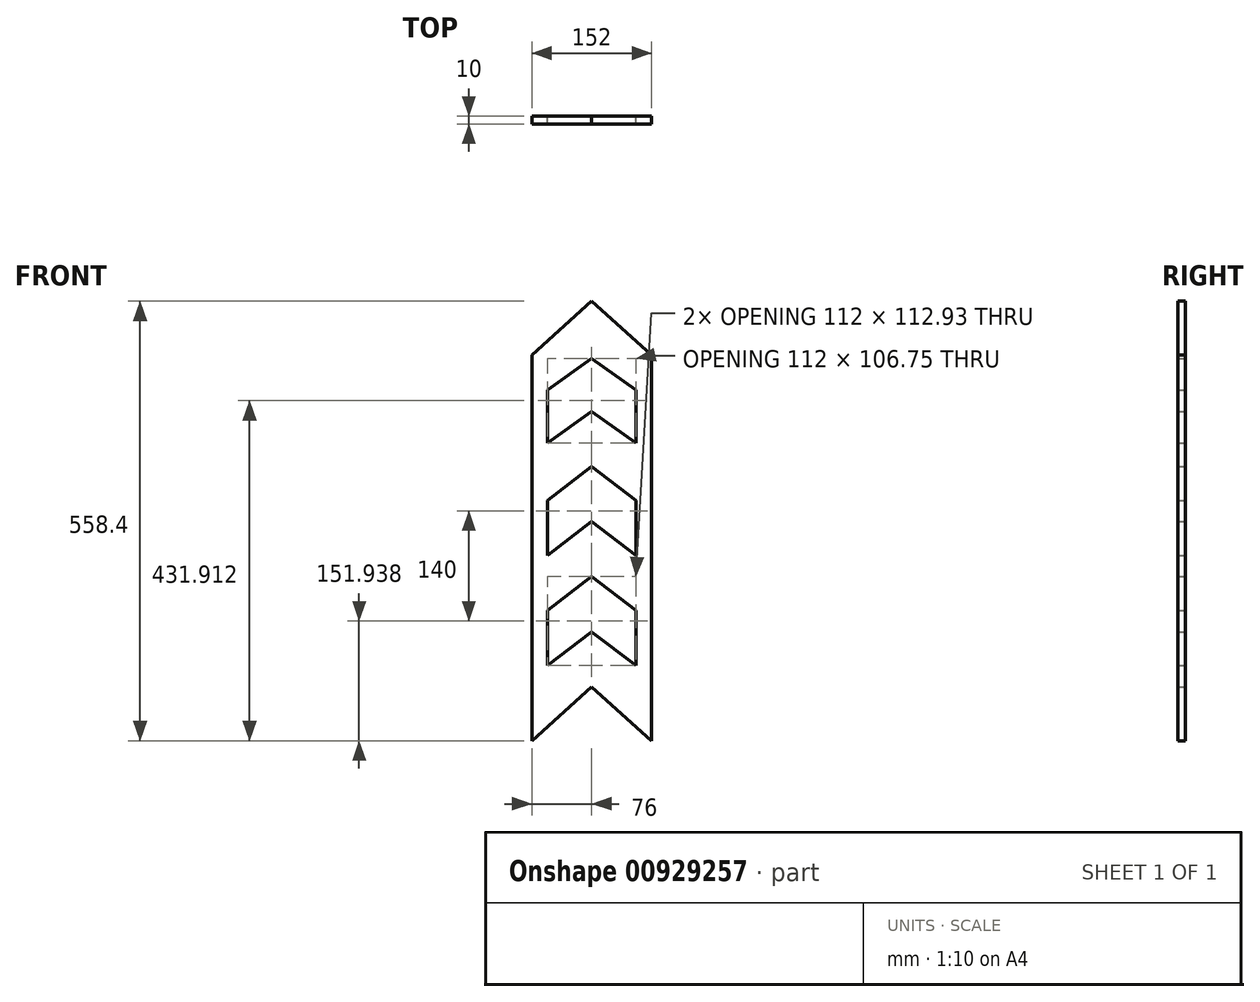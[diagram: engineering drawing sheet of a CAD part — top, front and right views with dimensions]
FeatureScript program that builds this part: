
annotation { "Feature Type Name" : "Feature", "Feature Type Description" : "" }
export const myFeature = defineFeature(function(context is Context, id is Id, definition is map)
    precondition{}
    {
        {
            var Q0;
            Q0=qCreatedBy(makeId("Front.planeOp"),FACE);
            var sketch = newSketch(context, id + "F0", { "sketchPlane" : qUnion([Q0])});
            skLineSegment(sketch, "E0", {"start": v(0, 241.08) * mm, "end": v(-76, 172.68) * mm});
            skLineSegment(sketch, "E1", {"start": v(-76, 172.68) * mm, "end": v(-76, -317.32) * mm});
            skLineSegment(sketch, "E2", {"start": v(-76, -317.32) * mm, "end": v(0, -248.92) * mm});
            skLineSegment(sketch, "E3", {"start": v(0, 167.96) * mm, "end": v(-56, 128.1) * mm});
            skLineSegment(sketch, "E4", {"start": v(-56, 128.1) * mm, "end": v(-56, 61.22) * mm});
            skLineSegment(sketch, "E5", {"start": v(-56, 61.22) * mm, "end": v(0, 101.08) * mm});
            skLineSegment(sketch, "E6", {"start": v(0, 31.08) * mm, "end": v(-56, -11.85) * mm});
            skLineSegment(sketch, "E7", {"start": v(-56, -11.85) * mm, "end": v(-56, -81.85) * mm});
            skLineSegment(sketch, "E8", {"start": v(-56, -81.85) * mm, "end": v(0, -38.92) * mm});
            skLineSegment(sketch, "E9", {"start": v(0, -108.92) * mm, "end": v(-56, -151.85) * mm});
            skLineSegment(sketch, "E10", {"start": v(-56, -151.85) * mm, "end": v(-56, -221.85) * mm});
            skLineSegment(sketch, "E11", {"start": v(-56, -221.85) * mm, "end": v(0, -178.92) * mm});
            skLineSegment(sketch, "E12.MirrorCS", {"start": v(0, 241.08) * mm, "end": v(76, 172.68) * mm});
            skLineSegment(sketch, "E13.MirrorCS", {"start": v(76, 172.68) * mm, "end": v(76, -317.32) * mm});
            skLineSegment(sketch, "E14.MirrorCS", {"start": v(56, 61.22) * mm, "end": v(0, 101.08) * mm});
            skLineSegment(sketch, "E15.MirrorCS", {"start": v(0, 31.08) * mm, "end": v(56, -11.85) * mm});
            skLineSegment(sketch, "E16.MirrorCS", {"start": v(56, -81.85) * mm, "end": v(0, -38.92) * mm});
            skLineSegment(sketch, "E17.MirrorCS", {"start": v(0, -108.92) * mm, "end": v(56, -151.85) * mm});
            skLineSegment(sketch, "E18.MirrorCS", {"start": v(76, -317.32) * mm, "end": v(0, -248.92) * mm});
            skLineSegment(sketch, "E19.MirrorCS", {"start": v(56, -221.85) * mm, "end": v(0, -178.92) * mm});
            skLineSegment(sketch, "E20.MirrorCS", {"start": v(0, 167.96) * mm, "end": v(56, 128.1) * mm});
            skLineSegment(sketch, "E21.MirrorCS", {"start": v(56, 128.1) * mm, "end": v(56, 61.22) * mm});
            skLineSegment(sketch, "E22.MirrorCS", {"start": v(56, -11.85) * mm, "end": v(56, -81.85) * mm});
            skLineSegment(sketch, "E23", {"start": v(56, -151.85) * mm, "end": v(56, -221.85) * mm});
            skSolve(sketch);
        }
        {
            var Q0;
            {var subQ1=sQuery(id+"F0.wireOp",EDGE,"E12.MirrorCS");Q0=makeQuery(id+"F0.imprint","IMPRINT",FACE,{"disambiguationData":[TD([[makeQuery(id+"F0.imprint","IMPRINT",EDGE,{"derivedFrom":subQ1}),-1.0]])]});}
            var Q1;
            {var subQ3=sQuery(id+"F0.wireOp",EDGE,"E0");Q1=makeQuery(id+"F0.imprint","IMPRINT",FACE,{"disambiguationData":[TD([[makeQuery(id+"F0.imprint","IMPRINT",EDGE,{"derivedFrom":subQ3}),1.0]])]});}
            var Q2;
            Q2=sQuery(id+"F0.wireOp",EDGE,"E9");
            extrude(context, id + "F1", {"entities" : qUnion([Q0, Q1]), "surfaceEntities" : qUnion([Q2]), "depth" : 10 * mm, "offsetDistance" : 25 * mm});
        }
    });
